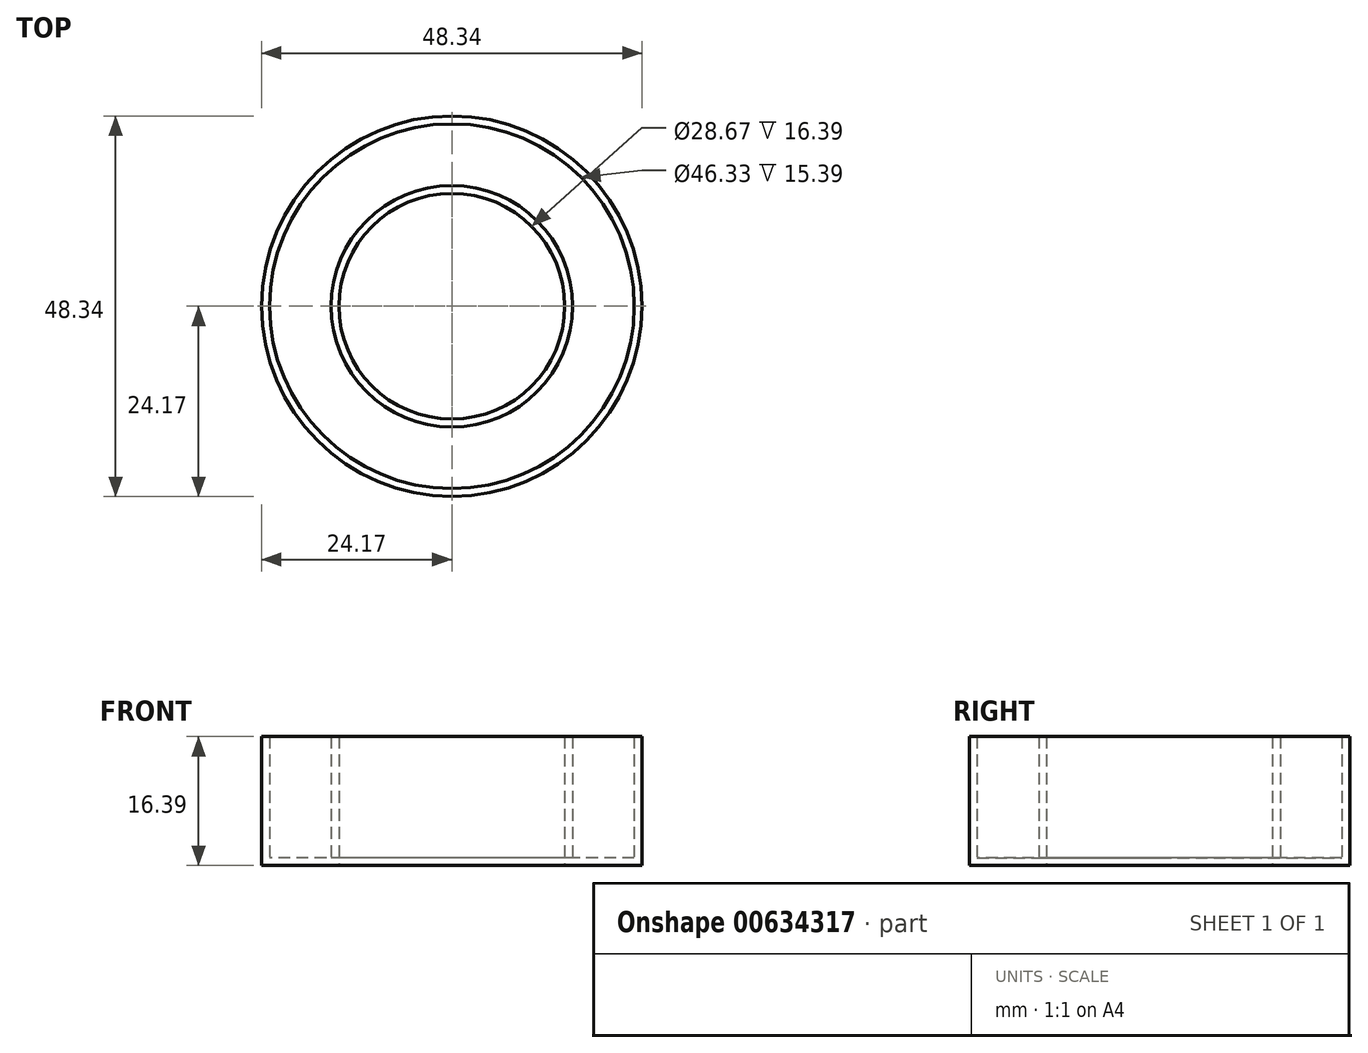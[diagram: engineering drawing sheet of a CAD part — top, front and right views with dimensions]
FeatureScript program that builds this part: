
annotation { "Feature Type Name" : "Feature", "Feature Type Description" : "" }
export const myFeature = defineFeature(function(context is Context, id is Id, definition is map)
    precondition{}
    {
        {
            var Q0;
            Q0=qCreatedBy(makeId("Top.planeOp"),FACE);
            var sketch = newSketch(context, id + "F0", { "sketchPlane" : qUnion([Q0])});
            skCircle(sketch, "E0", {"center": v(0, 0) * mm, "radius": 24.16 * mm});
            skCircle(sketch, "E1", {"center": v(0, 0) * mm, "radius": 14.34 * mm});
            skSolve(sketch);
        }
        {
            var Q0;
            Q0=makeQuery(id+"F0.imprint","IMPRINT",FACE,{"disambiguationData":[TD([[makeQuery(id+"F0.imprint","IMPRINT",EDGE,{"derivedFrom":sQuery(id+"F0.wireOp",EDGE,"E0")}),1.0]])]});
            extrude(context, id + "F1", {"entities" : qUnion([Q0]), "depth" : .1 * mm, "offsetDistance" : 25.4 * mm});
        }
        {
            var Q0;
            Q0=makeQuery(id+"F1.opExtrude","CAP_FACE",FACE,{"disambiguationData":[OSD([sQuery(id+"F0.wireOp",EDGE,"E0"),sQuery(id+"F0.wireOp",EDGE,"E1")])],"isStart":false});
            extrude(context, id + "F2", {"entities" : qUnion([Q0]), "operationType" : NewBodyOperationType.ADD, "depth" : 16.29 * mm, "offsetDistance" : 25.4 * mm});
        }
        {
            var Q0;
            Q0=makeQuery(id+"F2.opExtrude","CAP_FACE",FACE,{"disambiguationData":[OSD([sQuery(id+"F0.wireOp",EDGE,"E0"),sQuery(id+"F0.wireOp",EDGE,"E1")])],"isStart":false});
            shell(context, id + "F3", {"entities" : qUnion([Q0]), "thickness" : 1 * mm});
        }
    });
